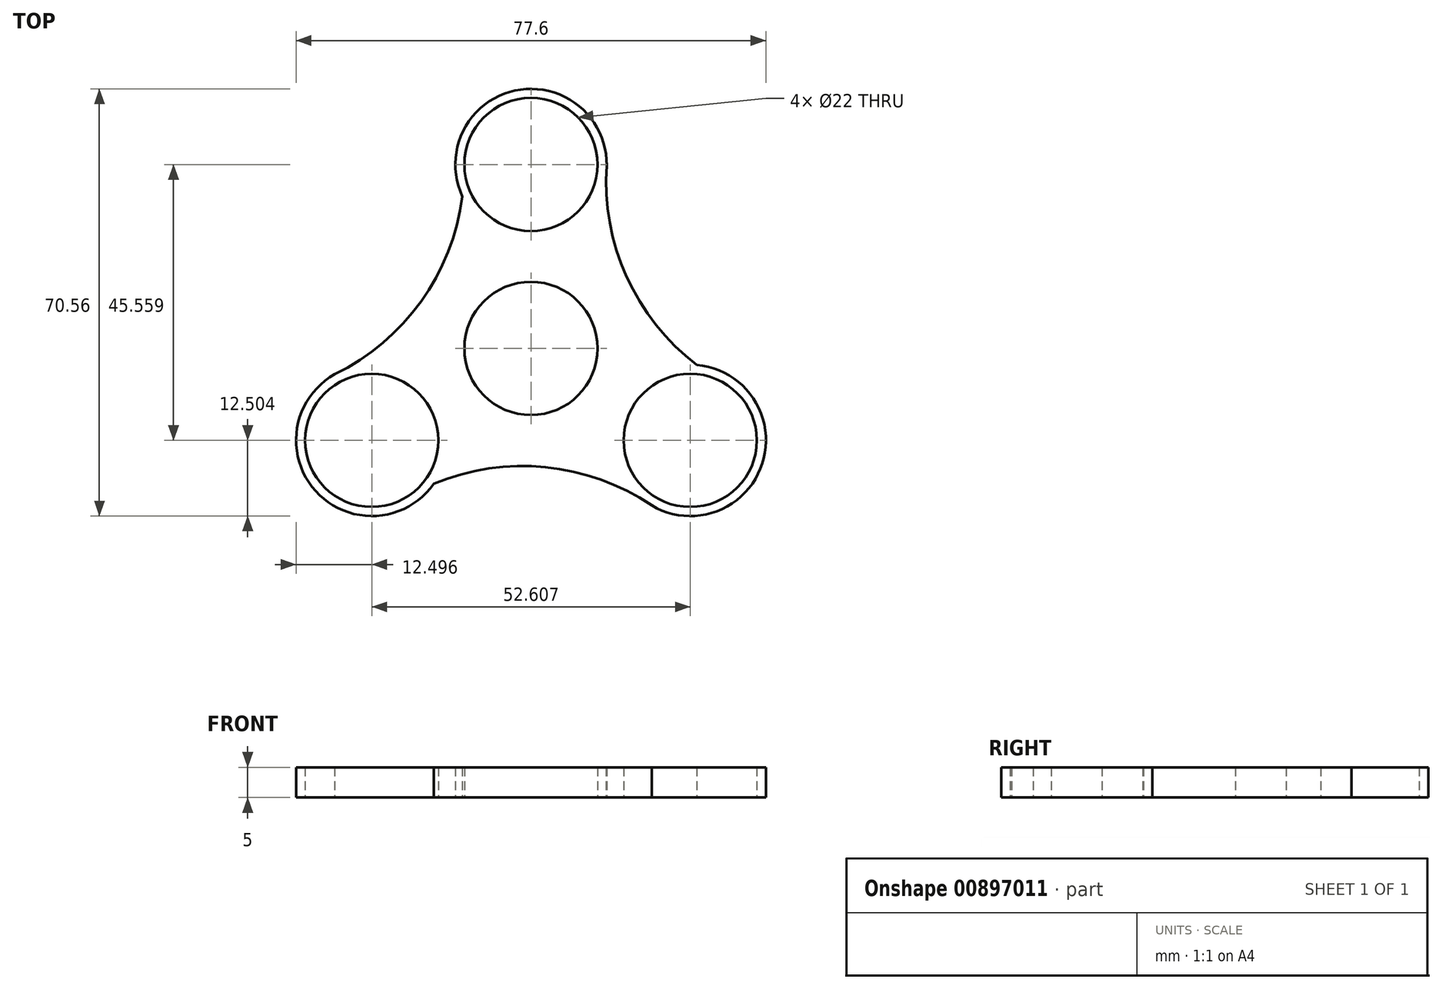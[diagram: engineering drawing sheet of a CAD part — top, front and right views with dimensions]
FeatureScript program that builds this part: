
annotation { "Feature Type Name" : "Feature", "Feature Type Description" : "" }
export const myFeature = defineFeature(function(context is Context, id is Id, definition is map)
    precondition{}
    {
        {
            var Q0;
            Q0=qCreatedBy(makeId("Top.planeOp"),FACE);
            var sketch = newSketch(context, id + "F0", { "sketchPlane" : qUnion([Q0])});
            skCircle(sketch, "E0", {"center": v(0, 0) * mm, "radius": 11 * mm});
            skCircle(sketch, "E1", {"center": v(0, 30.37) * mm, "radius": 11 * mm});
            skCircle(sketch, "E2.1.0", {"center": v(-26.3, -15.19) * mm, "radius": 11 * mm});
            skCircle(sketch, "E2.2.0", {"center": v(26.3, -15.19) * mm, "radius": 11 * mm});
            skCircle(sketch, "E3", {"center": v(0, 30.37) * mm, "radius": 12.5 * mm});
            skCircle(sketch, "E4.1.0", {"center": v(-26.3, -15.19) * mm, "radius": 12.5 * mm});
            skCircle(sketch, "E4.2.0", {"center": v(26.3, -15.19) * mm, "radius": 12.5 * mm});
            skArc(sketch, "E5", {"start": v(12.5, 30.22) * mm, "mid": v(15.8, 11.86) * mm, "end": v(27.4, -2.73) * mm});
            skArc(sketch, "E6.1.0", {"start": v(-32.42, -4.28) * mm, "mid": v(-18.17, 7.74) * mm, "end": v(-11.33, 25.09) * mm});
            skArc(sketch, "E6.2.0", {"start": v(19.92, -25.93) * mm, "mid": v(2.38, -19.6) * mm, "end": v(-16.06, -22.36) * mm});
            skSolve(sketch);
        }
        {
            var Q0;
            Q0=makeQuery(id+"F0.imprint","IMPRINT",FACE,{"disambiguationData":[TD([[makeQuery(id+"F0.imprint","IMPRINT",EDGE,{"derivedFrom":sQuery(id+"F0.wireOp",EDGE,"E0")}),-1.0]])]});
            var Q1;
            Q1=makeQuery(id+"F0.imprint","IMPRINT",FACE,{"disambiguationData":[TD([[makeQuery(id+"F0.imprint","IMPRINT",EDGE,{"derivedFrom":sQuery(id+"F0.wireOp",EDGE,"E1")}),-1.0]])]});
            var Q2;
            Q2=makeQuery(id+"F0.imprint","IMPRINT",FACE,{"disambiguationData":[TD([[makeQuery(id+"F0.imprint","IMPRINT",EDGE,{"derivedFrom":sQuery(id+"F0.wireOp",EDGE,"E2.2.0")}),-1.0]])]});
            var Q3;
            Q3=makeQuery(id+"F0.imprint","IMPRINT",FACE,{"disambiguationData":[TD([[makeQuery(id+"F0.imprint","IMPRINT",EDGE,{"derivedFrom":sQuery(id+"F0.wireOp",EDGE,"E2.1.0")}),-1.0]])]});
            extrude(context, id + "F1", {"entities" : qUnion([Q0, Q1, Q2, Q3]), "depth" : 5 * mm, "offsetDistance" : 25 * mm});
        }
    });
